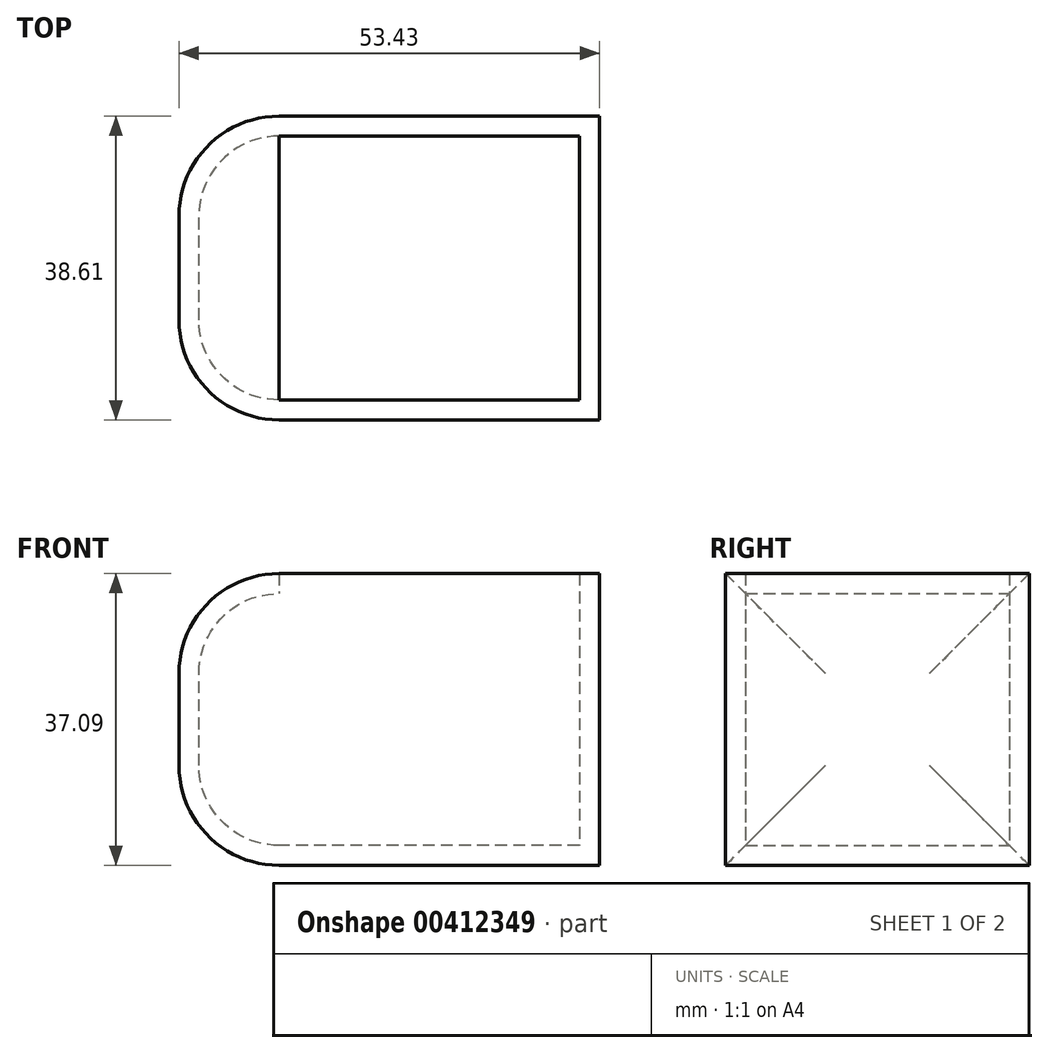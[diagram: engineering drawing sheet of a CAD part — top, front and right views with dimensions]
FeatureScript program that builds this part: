
annotation { "Feature Type Name" : "Feature", "Feature Type Description" : "" }
export const myFeature = defineFeature(function(context is Context, id is Id, definition is map)
    precondition{}
    {
        {
            var Q0;
            Q0=qCreatedBy(makeId("Top.planeOp"),FACE);
            var sketch = newSketch(context, id + "F0", { "sketchPlane" : qUnion([Q0])});
            skLineSegment(sketch, "E0.bottom", {"start": v(0, 0) * mm, "end": v(-53.43, 0) * mm});
            skLineSegment(sketch, "E0.top", {"start": v(0, 38.61) * mm, "end": v(-53.43, 38.61) * mm});
            skLineSegment(sketch, "E0.left", {"start": v(0, 0) * mm, "end": v(0, 38.61) * mm});
            skLineSegment(sketch, "E0.right", {"start": v(-53.43, 0) * mm, "end": v(-53.43, 38.61) * mm});
            skSolve(sketch);
        }
        {
            var Q0;
            Q0=makeQuery(id+"F0.imprint","IMPRINT",FACE,{"disambiguationData":[TD([[makeQuery(id+"F0.imprint","IMPRINT",EDGE,{"derivedFrom":sQuery(id+"F0.wireOp",EDGE,"E0.bottom")}),-1.0]])]});
            var Q1;
            Q1 = qSketchRegion(id + "F0", true);
            extrude(context, id + "F1", {"entities" : qUnion([Q0, Q1]), "depth" : 37.1 * mm});
        }
        {
            var Q0;
            Q0=makeQuery(id+"F1.opExtrude","SWEPT_FACE",FACE,{"disambiguationData":[OSD([sQuery(id+"F0.wireOp",EDGE,"E0.right")])]});
            fillet(context, id + "F2", {"entities" : qUnion([Q0]), "radius" : 12.7 * mm, "tangentPropagation" : true, "allowEdgeOverflow" : false});
        }
        {
            var Q0;
            Q0=makeQuery(id+"F1.opExtrude","CAP_FACE",FACE,{"disambiguationData":[OSD([sQuery(id+"F0.wireOp",EDGE,"E0.bottom"),sQuery(id+"F0.wireOp",EDGE,"E0.top"),sQuery(id+"F0.wireOp",EDGE,"E0.left"),sQuery(id+"F0.wireOp",EDGE,"E0.right")])],"isStart":false});
            shell(context, id + "F3", {"entities" : qUnion([Q0]), "thickness" : 2.54 * mm});
        }
    });
